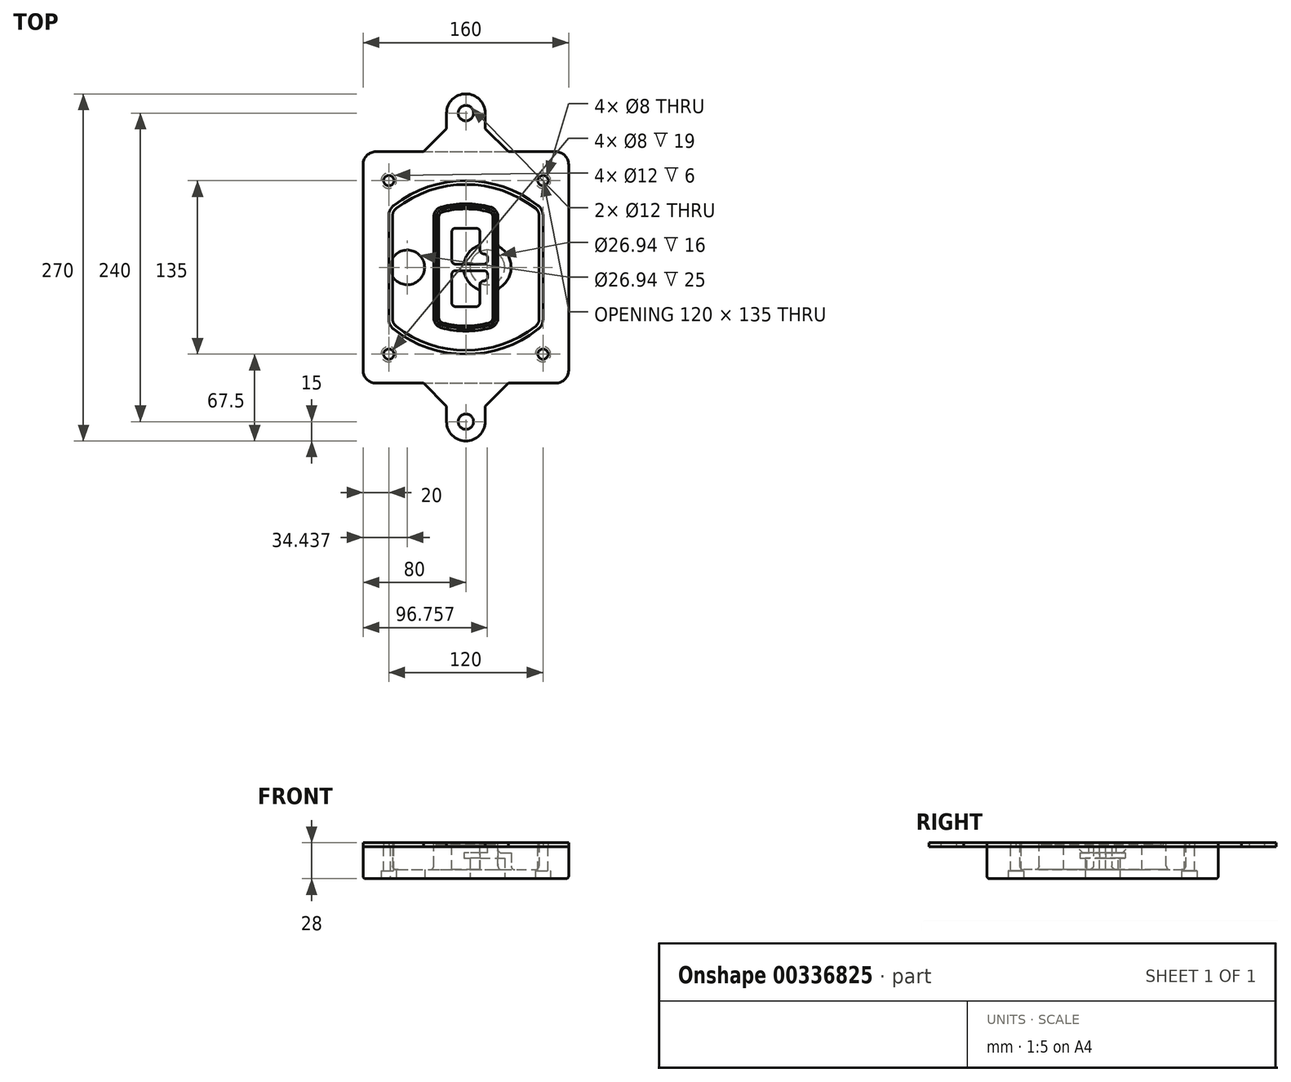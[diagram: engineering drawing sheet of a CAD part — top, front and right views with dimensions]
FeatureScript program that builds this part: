
annotation { "Feature Type Name" : "Feature", "Feature Type Description" : "" }
export const myFeature = defineFeature(function(context is Context, id is Id, definition is map)
    precondition{}
    {
        {
            var Q0;
            Q0=qCreatedBy(makeId("Top.planeOp"),FACE);
            var sketch = newSketch(context, id + "F0", { "sketchPlane" : qUnion([Q0])});
            skPoint(sketch, "E0.rect.middle", {"position": v(0, 0) * mm});
            skLineSegment(sketch, "E1.bottom", {"start": v(-70, -90) * mm, "end": v(70, -90) * mm});
            skLineSegment(sketch, "E1.top", {"start": v(-70, 90) * mm, "end": v(70, 90) * mm});
            skLineSegment(sketch, "E1.left", {"start": v(-80, -80) * mm, "end": v(-80, 80) * mm});
            skLineSegment(sketch, "E1.right", {"start": v(80, -80) * mm, "end": v(80, 80) * mm});
            skLineSegment(sketch, "E2", {"start": v(-80, 90) * mm, "end": v(80, -90) * mm, "construction": true});
            skLineSegment(sketch, "E3", {"start": v(80, 90) * mm, "end": v(-80, -90) * mm, "construction": true});
            skCircle(sketch, "E4", {"center": v(-60, 67.5) * mm, "radius": 4 * mm});
            skCircle(sketch, "E5", {"center": v(60, 67.5) * mm, "radius": 4 * mm});
            skCircle(sketch, "E6", {"center": v(60, -67.5) * mm, "radius": 4 * mm});
            skCircle(sketch, "E7", {"center": v(-60, -67.5) * mm, "radius": 4 * mm});
            skLineSegment(sketch, "E8", {"start": v(-60, 67.5) * mm, "end": v(60, 67.5) * mm, "construction": true});
            skLineSegment(sketch, "E9", {"start": v(60, 67.5) * mm, "end": v(60, -67.5) * mm, "construction": true});
            skLineSegment(sketch, "E10", {"start": v(60, -67.5) * mm, "end": v(-60, -67.5) * mm, "construction": true});
            skLineSegment(sketch, "E11", {"start": v(-60, -67.5) * mm, "end": v(-60, 67.5) * mm, "construction": true});
            skLineSegment(sketch, "E12", {"start": v(-60, 40.3) * mm, "end": v(-60, -40.3) * mm});
            skLineSegment(sketch, "E13", {"start": v(60, 40.3) * mm, "end": v(60, -40.3) * mm});
            skArc(sketch, "E14", {"start": v(56.15, 48.18) * mm, "mid": v(0, 67.5) * mm, "end": v(-56.15, 48.18) * mm});
            skArc(sketch, "E15", {"start": v(-56.15, -48.18) * mm, "mid": v(0, -67.5) * mm, "end": v(56.15, -48.18) * mm});
            skLineSegment(sketch, "E16", {"start": v(-60, 0) * mm, "end": v(60, 0) * mm, "construction": true});
            skPoint(sketch, "E17.visualSharp", {"position": v(-60, -45) * mm});
            skArc(sketch, "E17.filletArc", {"start": v(-60, -40.3) * mm, "mid": v(-58.99, -44.68) * mm, "end": v(-56.15, -48.18) * mm});
            skPoint(sketch, "E18.visualSharp", {"position": v(-60, 45) * mm});
            skArc(sketch, "E18.filletArc", {"start": v(-56.15, 48.18) * mm, "mid": v(-58.99, 44.68) * mm, "end": v(-60, 40.3) * mm});
            skPoint(sketch, "E19.visualSharp", {"position": v(60, 45) * mm});
            skArc(sketch, "E19.filletArc", {"start": v(60, 40.3) * mm, "mid": v(58.99, 44.68) * mm, "end": v(56.15, 48.18) * mm});
            skPoint(sketch, "E20.visualSharp", {"position": v(60, -45) * mm});
            skArc(sketch, "E20.filletArc", {"start": v(56.15, -48.18) * mm, "mid": v(58.99, -44.68) * mm, "end": v(60, -40.3) * mm});
            skPoint(sketch, "E21.visualSharp", {"position": v(-80, 90) * mm});
            skArc(sketch, "E21.filletArc", {"start": v(-70, 90) * mm, "mid": v(-77.07, 87.07) * mm, "end": v(-80, 80) * mm});
            skPoint(sketch, "E22.visualSharp", {"position": v(80, 90) * mm});
            skArc(sketch, "E22.filletArc", {"start": v(80, 80) * mm, "mid": v(77.07, 87.07) * mm, "end": v(70, 90) * mm});
            skPoint(sketch, "E23.visualSharp", {"position": v(80, -90) * mm});
            skArc(sketch, "E23.filletArc", {"start": v(70, -90) * mm, "mid": v(77.07, -87.07) * mm, "end": v(80, -80) * mm});
            skPoint(sketch, "E24.visualSharp", {"position": v(-80, -90) * mm});
            skArc(sketch, "E24.filletArc", {"start": v(-80, -80) * mm, "mid": v(-77.07, -87.07) * mm, "end": v(-70, -90) * mm});
            skArc(sketch, "E25.0", {"start": v(57, 40.3) * mm, "mid": v(56.3, 43.36) * mm, "end": v(54.3, 45.81) * mm});
            skLineSegment(sketch, "E25.1", {"start": v(57, 40.3) * mm, "end": v(57, -40.3) * mm});
            skArc(sketch, "E25.2", {"start": v(54.3, -45.81) * mm, "mid": v(56.3, -43.36) * mm, "end": v(57, -40.3) * mm});
            skArc(sketch, "E25.3", {"start": v(-54.3, -45.81) * mm, "mid": v(0, -64.5) * mm, "end": v(54.3, -45.81) * mm});
            skArc(sketch, "E25.4", {"start": v(-57, -40.3) * mm, "mid": v(-56.3, -43.36) * mm, "end": v(-54.3, -45.81) * mm});
            skArc(sketch, "E25.5", {"start": v(54.3, 45.81) * mm, "mid": v(0, 64.5) * mm, "end": v(-54.3, 45.81) * mm});
            skLineSegment(sketch, "E25.6", {"start": v(-57, 40.3) * mm, "end": v(-57, -40.3) * mm});
            skArc(sketch, "E25.7", {"start": v(-54.3, 45.81) * mm, "mid": v(-56.3, 43.36) * mm, "end": v(-57, 40.3) * mm});
            skArc(sketch, "E26.0", {"start": v(-58.62, 51.33) * mm, "mid": v(-62.58, 46.43) * mm, "end": v(-64, 40.3) * mm});
            skArc(sketch, "E26.1", {"start": v(58.62, 51.33) * mm, "mid": v(0, 71.5) * mm, "end": v(-58.62, 51.33) * mm});
            skArc(sketch, "E26.2", {"start": v(64, 40.3) * mm, "mid": v(62.58, 46.43) * mm, "end": v(58.62, 51.33) * mm});
            skLineSegment(sketch, "E26.3", {"start": v(64, 40.3) * mm, "end": v(64, -40.3) * mm});
            skArc(sketch, "E26.4", {"start": v(58.62, -51.33) * mm, "mid": v(62.58, -46.43) * mm, "end": v(64, -40.3) * mm});
            skLineSegment(sketch, "E26.5", {"start": v(-64, 40.3) * mm, "end": v(-64, -40.3) * mm});
            skArc(sketch, "E26.6", {"start": v(-58.62, -51.33) * mm, "mid": v(0, -71.5) * mm, "end": v(58.62, -51.33) * mm});
            skArc(sketch, "E26.7", {"start": v(-64, -40.3) * mm, "mid": v(-62.58, -46.43) * mm, "end": v(-58.62, -51.33) * mm});
            skSolve(sketch);
        }
        {
            var Q0;
            Q0=makeQuery(id+"F0.imprint","IMPRINT",FACE,{"disambiguationData":[TD([[makeQuery(id+"F0.imprint","IMPRINT",EDGE,{"derivedFrom":sQuery(id+"F0.wireOp",EDGE,"E1.bottom")}),1.0]])]});
            var Q1;
            Q1=makeQuery(id+"F0.imprint","IMPRINT",FACE,{"disambiguationData":[TD([[makeQuery(id+"F0.imprint","IMPRINT",EDGE,{"derivedFrom":sQuery(id+"F0.wireOp",EDGE,"E12")}),1.0]])]});
            var Q2;
            Q2=makeQuery(id+"F0.imprint","IMPRINT",FACE,{"disambiguationData":[TD([[makeQuery(id+"F0.imprint","IMPRINT",EDGE,{"derivedFrom":sQuery(id+"F0.wireOp",EDGE,"E25.0")}),1.0]])]});
            var Q3;
            Q3=makeQuery(id+"F0.imprint","IMPRINT",FACE,{"disambiguationData":[TD([[makeQuery(id+"F0.imprint","IMPRINT",EDGE,{"derivedFrom":sQuery(id+"F0.wireOp",EDGE,"E12")}),-1.0]])]});
            extrude(context, id + "F1", {"entities" : qUnion([Q0, Q1, Q2, Q3]), "oppositeDirection" : true, "depth" : 25 * mm});
        }
        {
            var Q0;
            Q0=makeQuery(id+"F0.imprint","IMPRINT",FACE,{"disambiguationData":[TD([[makeQuery(id+"F0.imprint","IMPRINT",EDGE,{"derivedFrom":sQuery(id+"F0.wireOp",EDGE,"E12")}),1.0]])]});
            extrude(context, id + "F2", {"entities" : qUnion([Q0]), "operationType" : NewBodyOperationType.ADD, "depth" : 3 * mm});
        }
        {
            var Q0;
            Q0=makeQuery(id+"F0.imprint","IMPRINT",FACE,{"disambiguationData":[TD([[makeQuery(id+"F0.imprint","IMPRINT",EDGE,{"derivedFrom":sQuery(id+"F0.wireOp",EDGE,"E25.0")}),1.0]])]});
            extrude(context, id + "F3", {"entities" : qUnion([Q0]), "operationType" : NewBodyOperationType.REMOVE, "oppositeDirection" : true, "depth" : 18 * mm});
        }
        {
            var Q0;
            Q0=makeQuery(id+"F2.opExtrude","CAP_FACE",FACE,{"disambiguationData":[OSD([sQuery(id+"F0.wireOp",EDGE,"E12"),sQuery(id+"F0.wireOp",EDGE,"E13"),sQuery(id+"F0.wireOp",EDGE,"E14"),sQuery(id+"F0.wireOp",EDGE,"E15"),sQuery(id+"F0.wireOp",EDGE,"E17.filletArc"),sQuery(id+"F0.wireOp",EDGE,"E18.filletArc"),sQuery(id+"F0.wireOp",EDGE,"E19.filletArc"),sQuery(id+"F0.wireOp",EDGE,"E20.filletArc"),sQuery(id+"F0.wireOp",EDGE,"E25.0"),sQuery(id+"F0.wireOp",EDGE,"E25.1"),sQuery(id+"F0.wireOp",EDGE,"E25.2"),sQuery(id+"F0.wireOp",EDGE,"E25.3"),sQuery(id+"F0.wireOp",EDGE,"E25.4"),sQuery(id+"F0.wireOp",EDGE,"E25.5"),sQuery(id+"F0.wireOp",EDGE,"E25.6"),sQuery(id+"F0.wireOp",EDGE,"E25.7")])],"isStart":false});
            var sketch = newSketch(context, id + "F4", { "sketchPlane" : qUnion([Q0])});
            skArc(sketch, "E27.0", {"start": v(-19.08, -46.97) * mm, "mid": v(0, -49.5) * mm, "end": v(19.08, -46.97) * mm});
            skArc(sketch, "E28.0", {"start": v(19.08, 46.97) * mm, "mid": v(0, 49.5) * mm, "end": v(-19.08, 46.97) * mm});
            skLineSegment(sketch, "E29", {"start": v(-25, 39.25) * mm, "end": v(-25, -39.25) * mm});
            skLineSegment(sketch, "E30", {"start": v(25, 39.25) * mm, "end": v(25, -39.25) * mm});
            skLineSegment(sketch, "E31", {"start": v(-25, 45.1) * mm, "end": v(25, 45.1) * mm, "construction": true});
            skLineSegment(sketch, "E32", {"start": v(-25, -45.1) * mm, "end": v(25, -45.1) * mm, "construction": true});
            skPoint(sketch, "E33.visualSharp", {"position": v(-25, 45.1) * mm});
            skArc(sketch, "E33.filletArc", {"start": v(-19.08, 46.97) * mm, "mid": v(-23.35, 44.11) * mm, "end": v(-25, 39.25) * mm});
            skPoint(sketch, "E34.visualSharp", {"position": v(25, 45.1) * mm});
            skArc(sketch, "E34.filletArc", {"start": v(25, 39.25) * mm, "mid": v(23.35, 44.11) * mm, "end": v(19.08, 46.97) * mm});
            skPoint(sketch, "E35.visualSharp", {"position": v(25, -45.1) * mm});
            skArc(sketch, "E35.filletArc", {"start": v(19.08, -46.97) * mm, "mid": v(23.35, -44.11) * mm, "end": v(25, -39.25) * mm});
            skPoint(sketch, "E36.visualSharp", {"position": v(-25, -45.1) * mm});
            skArc(sketch, "E36.filletArc", {"start": v(-25, -39.25) * mm, "mid": v(-23.35, -44.11) * mm, "end": v(-19.08, -46.97) * mm});
            skArc(sketch, "E37.0", {"start": v(54.3, 45.81) * mm, "mid": v(0, 64.5) * mm, "end": v(-54.3, 45.81) * mm});
            skArc(sketch, "E37.1", {"start": v(-54.3, 45.81) * mm, "mid": v(-56.3, 43.36) * mm, "end": v(-57, 40.3) * mm});
            skLineSegment(sketch, "E37.2", {"start": v(-57, 40.3) * mm, "end": v(-57, -40.3) * mm});
            skArc(sketch, "E37.3", {"start": v(-57, -40.3) * mm, "mid": v(-56.3, -43.36) * mm, "end": v(-54.3, -45.81) * mm});
            skArc(sketch, "E37.4", {"start": v(-54.3, -45.81) * mm, "mid": v(0, -64.5) * mm, "end": v(54.3, -45.81) * mm});
            skArc(sketch, "E37.5", {"start": v(54.3, -45.81) * mm, "mid": v(56.3, -43.36) * mm, "end": v(57, -40.3) * mm});
            skLineSegment(sketch, "E37.6", {"start": v(57, 40.3) * mm, "end": v(57, -40.3) * mm});
            skArc(sketch, "E37.7", {"start": v(57, 40.3) * mm, "mid": v(56.3, 43.36) * mm, "end": v(54.3, 45.81) * mm});
            skLineSegment(sketch, "E38.0", {"start": v(23, 39.25) * mm, "end": v(23, -39.25) * mm});
            skArc(sketch, "E38.1", {"start": v(18.56, -45.04) * mm, "mid": v(21.76, -42.9) * mm, "end": v(23, -39.25) * mm});
            skArc(sketch, "E38.2", {"start": v(-18.56, -45.04) * mm, "mid": v(0, -47.5) * mm, "end": v(18.56, -45.04) * mm});
            skArc(sketch, "E38.3", {"start": v(-23, -39.25) * mm, "mid": v(-21.76, -42.9) * mm, "end": v(-18.56, -45.04) * mm});
            skLineSegment(sketch, "E38.4", {"start": v(-23, 39.25) * mm, "end": v(-23, -39.25) * mm});
            skArc(sketch, "E38.5", {"start": v(23, 39.25) * mm, "mid": v(21.76, 42.9) * mm, "end": v(18.56, 45.04) * mm});
            skArc(sketch, "E38.6", {"start": v(-18.56, 45.04) * mm, "mid": v(-21.76, 42.9) * mm, "end": v(-23, 39.25) * mm});
            skArc(sketch, "E38.7", {"start": v(18.56, 45.04) * mm, "mid": v(0, 47.5) * mm, "end": v(-18.56, 45.04) * mm});
            skArc(sketch, "E39.0", {"start": v(21, 39.25) * mm, "mid": v(20.18, 41.68) * mm, "end": v(18.04, 43.1) * mm});
            skLineSegment(sketch, "E39.1", {"start": v(21, 39.25) * mm, "end": v(21, -39.25) * mm});
            skArc(sketch, "E39.2", {"start": v(18.04, -43.1) * mm, "mid": v(20.18, -41.68) * mm, "end": v(21, -39.25) * mm});
            skArc(sketch, "E39.3", {"start": v(-18.04, -43.1) * mm, "mid": v(0, -45.5) * mm, "end": v(18.04, -43.1) * mm});
            skArc(sketch, "E39.4", {"start": v(-21, -39.25) * mm, "mid": v(-20.18, -41.68) * mm, "end": v(-18.04, -43.1) * mm});
            skArc(sketch, "E39.5", {"start": v(18.04, 43.1) * mm, "mid": v(0, 45.5) * mm, "end": v(-18.04, 43.1) * mm});
            skLineSegment(sketch, "E39.6", {"start": v(-21, 39.25) * mm, "end": v(-21, -39.25) * mm});
            skArc(sketch, "E39.7", {"start": v(-18.04, 43.1) * mm, "mid": v(-20.18, 41.68) * mm, "end": v(-21, 39.25) * mm});
            skLineSegment(sketch, "E40", {"start": v(-25, 0) * mm, "end": v(25, 0) * mm, "construction": true});
            skLineSegment(sketch, "E41", {"start": v(-11, 5.5) * mm, "end": v(-11, 27.5) * mm});
            skLineSegment(sketch, "E42", {"start": v(-8, 30.5) * mm, "end": v(8, 30.5) * mm});
            skLineSegment(sketch, "E43", {"start": v(11, 27.5) * mm, "end": v(11, 13.5) * mm});
            skLineSegment(sketch, "E44", {"start": v(14, 10.5) * mm, "end": v(14, 10.5) * mm});
            skLineSegment(sketch, "E45", {"start": v(17, 7.5) * mm, "end": v(17, 5.5) * mm});
            skLineSegment(sketch, "E46", {"start": v(14, 2.5) * mm, "end": v(-8, 2.5) * mm});
            skPoint(sketch, "E47.visualSharp", {"position": v(-11, 30.5) * mm});
            skArc(sketch, "E47.filletArc", {"start": v(-8, 30.5) * mm, "mid": v(-10.12, 29.62) * mm, "end": v(-11, 27.5) * mm});
            skPoint(sketch, "E48.visualSharp", {"position": v(11, 30.5) * mm});
            skArc(sketch, "E48.filletArc", {"start": v(11, 27.5) * mm, "mid": v(10.12, 29.62) * mm, "end": v(8, 30.5) * mm});
            skPoint(sketch, "E49.visualSharp", {"position": v(11, 10.5) * mm});
            skArc(sketch, "E49.filletArc", {"start": v(11, 13.5) * mm, "mid": v(11.88, 11.38) * mm, "end": v(14, 10.5) * mm});
            skPoint(sketch, "E50.visualSharp", {"position": v(17, 10.5) * mm});
            skArc(sketch, "E50.filletArc", {"start": v(17, 7.5) * mm, "mid": v(16.12, 9.62) * mm, "end": v(14, 10.5) * mm});
            skPoint(sketch, "E51.visualSharp", {"position": v(17, 2.5) * mm});
            skArc(sketch, "E51.filletArc", {"start": v(14, 2.5) * mm, "mid": v(16.12, 3.38) * mm, "end": v(17, 5.5) * mm});
            skPoint(sketch, "E52.visualSharp", {"position": v(-11, 2.5) * mm});
            skArc(sketch, "E52.filletArc", {"start": v(-11, 5.5) * mm, "mid": v(-10.12, 3.38) * mm, "end": v(-8, 2.5) * mm});
            skLineSegment(sketch, "E53.0.MirrorCS", {"start": v(14, -2.5) * mm, "end": v(-8, -2.5) * mm});
            skArc(sketch, "E54.0.MirrorCS", {"start": v(-11, -5.5) * mm, "mid": v(-10.12, -3.38) * mm, "end": v(-8, -2.5) * mm});
            skLineSegment(sketch, "E55.0.MirrorCS", {"start": v(-11, -5.5) * mm, "end": v(-11, -27.5) * mm});
            skArc(sketch, "E56.0.MirrorCS", {"start": v(-8, -30.5) * mm, "mid": v(-10.12, -29.62) * mm, "end": v(-11, -27.5) * mm});
            skLineSegment(sketch, "E57.0.MirrorCS", {"start": v(-8, -30.5) * mm, "end": v(8, -30.5) * mm});
            skArc(sketch, "E58.0.MirrorCS", {"start": v(11, -27.5) * mm, "mid": v(10.12, -29.62) * mm, "end": v(8, -30.5) * mm});
            skLineSegment(sketch, "E59.0.MirrorCS", {"start": v(11, -27.5) * mm, "end": v(11, -13.5) * mm});
            skArc(sketch, "E60.0.MirrorCS", {"start": v(11, -13.5) * mm, "mid": v(11.88, -11.38) * mm, "end": v(14, -10.5) * mm});
            skArc(sketch, "E61.0.MirrorCS", {"start": v(17, -7.5) * mm, "mid": v(16.12, -9.62) * mm, "end": v(14, -10.5) * mm});
            skLineSegment(sketch, "E62.0.MirrorCS", {"start": v(17, -7.5) * mm, "end": v(17, -5.5) * mm});
            skArc(sketch, "E63.0.MirrorCS", {"start": v(14, -2.5) * mm, "mid": v(16.12, -3.38) * mm, "end": v(17, -5.5) * mm});
            skSolve(sketch);
        }
        {
            var Q0;
            Q0=makeQuery(id+"F4.imprint","IMPRINT",FACE,{"disambiguationData":[TD([[makeQuery(id+"F4.imprint","IMPRINT",EDGE,{"derivedFrom":sQuery(id+"F4.wireOp",EDGE,"E27.0")}),1.0]])]});
            var Q1;
            Q1=makeQuery(id+"F4.imprint","IMPRINT",FACE,{"disambiguationData":[TD([[makeQuery(id+"F4.imprint","IMPRINT",EDGE,{"derivedFrom":sQuery(id+"F4.wireOp",EDGE,"E38.0")}),-1.0]])]});
            var Q2;
            Q2=makeQuery(id+"F4.imprint","IMPRINT",FACE,{"disambiguationData":[TD([[makeQuery(id+"F4.imprint","IMPRINT",EDGE,{"derivedFrom":sQuery(id+"F4.wireOp",EDGE,"E39.0")}),1.0]])]});
            extrude(context, id + "F5", {"entities" : qUnion([Q0, Q1, Q2]), "operationType" : NewBodyOperationType.ADD, "endBound" : BoundingType.UP_TO_NEXT, "oppositeDirection" : true, "depth" : 25 * mm});
        }
        {
            var Q0;
            Q0=makeQuery(id+"F4.imprint","IMPRINT",FACE,{"disambiguationData":[TD([[makeQuery(id+"F4.imprint","IMPRINT",EDGE,{"derivedFrom":sQuery(id+"F4.wireOp",EDGE,"E38.0")}),-1.0]])]});
            extrude(context, id + "F6", {"entities" : qUnion([Q0]), "operationType" : NewBodyOperationType.REMOVE, "oppositeDirection" : true, "depth" : 2 * mm});
        }
        {
            var Q0;
            Q0=makeQuery(id+"F1.opExtrude","CAP_FACE",FACE,{"disambiguationData":[OSD([sQuery(id+"F0.wireOp",EDGE,"E1.bottom"),sQuery(id+"F0.wireOp",EDGE,"E1.top"),sQuery(id+"F0.wireOp",EDGE,"E1.left"),sQuery(id+"F0.wireOp",EDGE,"E1.right"),sQuery(id+"F0.wireOp",EDGE,"E4"),sQuery(id+"F0.wireOp",EDGE,"E5"),sQuery(id+"F0.wireOp",EDGE,"E6"),sQuery(id+"F0.wireOp",EDGE,"E7"),sQuery(id+"F0.wireOp",EDGE,"E21.filletArc"),sQuery(id+"F0.wireOp",EDGE,"E22.filletArc"),sQuery(id+"F0.wireOp",EDGE,"E23.filletArc"),sQuery(id+"F0.wireOp",EDGE,"E24.filletArc")])],"isStart":false});
            var sketch = newSketch(context, id + "F7", { "sketchPlane" : qUnion([Q0])});
            skCircle(sketch, "E64", {"center": v(16.76, 0) * mm, "radius": 13.47 * mm});
            skCircle(sketch, "E65", {"center": v(-45.56, 0) * mm, "radius": 13.47 * mm});
            skLineSegment(sketch, "E66", {"start": v(80, 0) * mm, "end": v(-80, 0) * mm});
            skCircle(sketch, "E67", {"center": v(16.76, 0) * mm, "radius": 18.47 * mm});
            skCircle(sketch, "E68", {"center": v(60, -67.5) * mm, "radius": 6 * mm});
            skCircle(sketch, "E69", {"center": v(-60, -67.5) * mm, "radius": 6 * mm});
            skCircle(sketch, "E70", {"center": v(-60, 67.5) * mm, "radius": 6 * mm});
            skCircle(sketch, "E71", {"center": v(60, 67.5) * mm, "radius": 6 * mm});
            skSolve(sketch);
        }
        {
            var Q0;
            {var subQ1=sQuery(id+"F7.wireOp",EDGE,"E66");var subQ4=sQuery(id+"F7.wireOp",EDGE,"E64");var subQ6=makeQuery(id+"F7.imprint","INTERSECT",VERTEX,{"disambiguationData":[OD(0.0)],"derivedFrom":[subQ4,subQ1]});Q0=makeQuery(id+"F7.imprint","IMPRINT",FACE,{"disambiguationData":[TD([[makeQuery(id+"F7.imprint","IMPRINT",EDGE,{"disambiguationData":[TD([[subQ6,-1.0]])],"derivedFrom":subQ4}),-1.0]])]});}
            var Q1;
            {var subQ0=sQuery(id+"F7.wireOp",EDGE,"E66");var subQ1=sQuery(id+"F7.wireOp",EDGE,"E64");var subQ3=makeQuery(id+"F7.imprint","INTERSECT",VERTEX,{"disambiguationData":[OD(0.0)],"derivedFrom":[subQ1,subQ0]});Q1=makeQuery(id+"F7.imprint","IMPRINT",FACE,{"disambiguationData":[TD([[makeQuery(id+"F7.imprint","IMPRINT",EDGE,{"disambiguationData":[TD([[subQ3,-1.0]])],"derivedFrom":subQ1}),1.0]])]});}
            var Q2;
            {var subQ0=sQuery(id+"F7.wireOp",EDGE,"E66");var subQ1=sQuery(id+"F7.wireOp",EDGE,"E64");var subQ3=makeQuery(id+"F7.imprint","INTERSECT",VERTEX,{"disambiguationData":[OD(0.0)],"derivedFrom":[subQ1,subQ0]});Q2=makeQuery(id+"F7.imprint","IMPRINT",FACE,{"disambiguationData":[TD([[makeQuery(id+"F7.imprint","IMPRINT",EDGE,{"disambiguationData":[TD([[subQ3,1.0]])],"derivedFrom":subQ1}),1.0]])]});}
            var Q3;
            {var subQ1=sQuery(id+"F7.wireOp",EDGE,"E66");var subQ4=sQuery(id+"F7.wireOp",EDGE,"E64");var subQ6=makeQuery(id+"F7.imprint","INTERSECT",VERTEX,{"disambiguationData":[OD(0.0)],"derivedFrom":[subQ4,subQ1]});Q3=makeQuery(id+"F7.imprint","IMPRINT",FACE,{"disambiguationData":[TD([[makeQuery(id+"F7.imprint","IMPRINT",EDGE,{"disambiguationData":[TD([[subQ6,1.0]])],"derivedFrom":subQ4}),-1.0]])]});}
            extrude(context, id + "F8", {"entities" : qUnion([Q0, Q1, Q2, Q3]), "operationType" : NewBodyOperationType.ADD, "oppositeDirection" : true, "depth" : 20 * mm});
        }
        {
            var Q0;
            {var subQ0=sQuery(id+"F7.wireOp",EDGE,"E66");var subQ1=sQuery(id+"F7.wireOp",EDGE,"E64");var subQ3=makeQuery(id+"F7.imprint","INTERSECT",VERTEX,{"disambiguationData":[OD(0.0)],"derivedFrom":[subQ1,subQ0]});Q0=makeQuery(id+"F7.imprint","IMPRINT",FACE,{"disambiguationData":[TD([[makeQuery(id+"F7.imprint","IMPRINT",EDGE,{"disambiguationData":[TD([[subQ3,-1.0]])],"derivedFrom":subQ1}),1.0]])]});}
            var Q1;
            {var subQ0=sQuery(id+"F7.wireOp",EDGE,"E66");var subQ1=sQuery(id+"F7.wireOp",EDGE,"E64");var subQ3=makeQuery(id+"F7.imprint","INTERSECT",VERTEX,{"disambiguationData":[OD(0.0)],"derivedFrom":[subQ1,subQ0]});Q1=makeQuery(id+"F7.imprint","IMPRINT",FACE,{"disambiguationData":[TD([[makeQuery(id+"F7.imprint","IMPRINT",EDGE,{"disambiguationData":[TD([[subQ3,1.0]])],"derivedFrom":subQ1}),1.0]])]});}
            extrude(context, id + "F9", {"entities" : qUnion([Q0, Q1]), "operationType" : NewBodyOperationType.REMOVE, "oppositeDirection" : true, "depth" : 16 * mm});
        }
        {
            var Q0;
            {var subQ0=sQuery(id+"F7.wireOp",EDGE,"E66");var subQ1=sQuery(id+"F7.wireOp",EDGE,"E65");var subQ3=makeQuery(id+"F7.imprint","INTERSECT",VERTEX,{"disambiguationData":[OD(0.0)],"derivedFrom":[subQ1,subQ0]});Q0=makeQuery(id+"F7.imprint","IMPRINT",FACE,{"disambiguationData":[TD([[makeQuery(id+"F7.imprint","IMPRINT",EDGE,{"disambiguationData":[TD([[subQ3,-1.0]])],"derivedFrom":subQ1}),1.0]])]});}
            var Q1;
            {var subQ0=sQuery(id+"F7.wireOp",EDGE,"E66");var subQ1=sQuery(id+"F7.wireOp",EDGE,"E65");var subQ3=makeQuery(id+"F7.imprint","INTERSECT",VERTEX,{"disambiguationData":[OD(0.0)],"derivedFrom":[subQ1,subQ0]});Q1=makeQuery(id+"F7.imprint","IMPRINT",FACE,{"disambiguationData":[TD([[makeQuery(id+"F7.imprint","IMPRINT",EDGE,{"disambiguationData":[TD([[subQ3,1.0]])],"derivedFrom":subQ1}),1.0]])]});}
            extrude(context, id + "F10", {"entities" : qUnion([Q0, Q1]), "operationType" : NewBodyOperationType.REMOVE, "oppositeDirection" : true, "depth" : 25 * mm});
        }
        {
            var Q0;
            Q0=makeQuery(id+"F7.imprint","IMPRINT",FACE,{"disambiguationData":[TD([[makeQuery(id+"F7.imprint","IMPRINT",EDGE,{"derivedFrom":sQuery(id+"F7.wireOp",EDGE,"E68")}),1.0]])]});
            var Q1;
            Q1=makeQuery(id+"F7.imprint","IMPRINT",FACE,{"disambiguationData":[TD([[makeQuery(id+"F7.imprint","IMPRINT",EDGE,{"derivedFrom":makeQuery(id+"F1.opExtrude","CAP_EDGE",EDGE,{"disambiguationData":[OSD([sQuery(id+"F0.wireOp",EDGE,"E5")])],"isStart":false})}),-1.0]])]});
            var Q2;
            Q2=makeQuery(id+"F7.imprint","IMPRINT",FACE,{"disambiguationData":[TD([[makeQuery(id+"F7.imprint","IMPRINT",EDGE,{"derivedFrom":sQuery(id+"F7.wireOp",EDGE,"E69")}),1.0]])]});
            var Q3;
            Q3=makeQuery(id+"F7.imprint","IMPRINT",FACE,{"disambiguationData":[TD([[makeQuery(id+"F7.imprint","IMPRINT",EDGE,{"derivedFrom":makeQuery(id+"F1.opExtrude","CAP_EDGE",EDGE,{"disambiguationData":[OSD([sQuery(id+"F0.wireOp",EDGE,"E4")])],"isStart":false})}),-1.0]])]});
            var Q4;
            Q4=makeQuery(id+"F7.imprint","IMPRINT",FACE,{"disambiguationData":[TD([[makeQuery(id+"F7.imprint","IMPRINT",EDGE,{"derivedFrom":sQuery(id+"F7.wireOp",EDGE,"E70")}),1.0]])]});
            var Q5;
            Q5=makeQuery(id+"F7.imprint","IMPRINT",FACE,{"disambiguationData":[TD([[makeQuery(id+"F7.imprint","IMPRINT",EDGE,{"derivedFrom":makeQuery(id+"F1.opExtrude","CAP_EDGE",EDGE,{"disambiguationData":[OSD([sQuery(id+"F0.wireOp",EDGE,"E7")])],"isStart":false})}),-1.0]])]});
            var Q6;
            Q6=makeQuery(id+"F7.imprint","IMPRINT",FACE,{"disambiguationData":[TD([[makeQuery(id+"F7.imprint","IMPRINT",EDGE,{"derivedFrom":sQuery(id+"F7.wireOp",EDGE,"E71")}),1.0]])]});
            var Q7;
            Q7=makeQuery(id+"F7.imprint","IMPRINT",FACE,{"disambiguationData":[TD([[makeQuery(id+"F7.imprint","IMPRINT",EDGE,{"derivedFrom":makeQuery(id+"F1.opExtrude","CAP_EDGE",EDGE,{"disambiguationData":[OSD([sQuery(id+"F0.wireOp",EDGE,"E6")])],"isStart":false})}),-1.0]])]});
            extrude(context, id + "F11", {"entities" : qUnion([Q0, Q1, Q2, Q3, Q4, Q5, Q6, Q7]), "operationType" : NewBodyOperationType.REMOVE, "oppositeDirection" : true, "depth" : 6 * mm});
        }
        {
            var Q0;
            Q0=makeQuery(id+"F9.boolean.opBoolean","COPY",FACE,{"derivedFrom":makeQuery(id+"F9.opExtrude","CAP_FACE",FACE,{"disambiguationData":[OSD([sQuery(id+"F7.wireOp",EDGE,"E64")])],"isStart":false})});
            var sketch = newSketch(context, id + "F12", { "sketchPlane" : qUnion([Q0])});
            skArc(sketch, "E72.0", {"start": v(11, 17.55) * mm, "mid": v(2.57, 11.82) * mm, "end": v(-1.54, 2.5) * mm});
            skArc(sketch, "E72.1", {"start": v(-1.54, -2.5) * mm, "mid": v(2.57, -11.82) * mm, "end": v(11, -17.55) * mm});
            skLineSegment(sketch, "E73", {"start": v(-1.54, -2.5) * mm, "end": v(14, -2.5) * mm});
            skLineSegment(sketch, "E74.0", {"start": v(14, 2.5) * mm, "end": v(-1.54, 2.5) * mm});
            skArc(sketch, "E74.1", {"start": v(14, 2.5) * mm, "mid": v(16.12, 3.38) * mm, "end": v(17, 5.5) * mm});
            skLineSegment(sketch, "E74.2", {"start": v(17, 7.5) * mm, "end": v(17, 5.5) * mm});
            skArc(sketch, "E74.3", {"start": v(17, 7.5) * mm, "mid": v(16.12, 9.62) * mm, "end": v(14, 10.5) * mm});
            skArc(sketch, "E74.4", {"start": v(11, 13.5) * mm, "mid": v(11.88, 11.38) * mm, "end": v(14, 10.5) * mm});
            skLineSegment(sketch, "E74.5", {"start": v(11, 17.55) * mm, "end": v(11, 13.5) * mm});
            skLineSegment(sketch, "E74.7", {"start": v(14, -2.5) * mm, "end": v(-1.54, -2.5) * mm});
            skArc(sketch, "E74.8", {"start": v(14, -2.5) * mm, "mid": v(16.12, -3.38) * mm, "end": v(17, -5.5) * mm});
            skLineSegment(sketch, "E74.9", {"start": v(17, -7.5) * mm, "end": v(17, -5.5) * mm});
            skArc(sketch, "E74.10", {"start": v(17, -7.5) * mm, "mid": v(16.12, -9.62) * mm, "end": v(14, -10.5) * mm});
            skArc(sketch, "E74.11", {"start": v(11, -13.5) * mm, "mid": v(11.88, -11.38) * mm, "end": v(14, -10.5) * mm});
            skLineSegment(sketch, "E74.12", {"start": v(11, -17.55) * mm, "end": v(11, -13.5) * mm});
            skPoint(sketch, "E75.orphan", {"position": v(11, -27.5) * mm});
            skPoint(sketch, "E76.orphan", {"position": v(-8, -2.5) * mm});
            skPoint(sketch, "E77.orphan", {"position": v(-8, 2.5) * mm});
            skPoint(sketch, "E78.orphan", {"position": v(11, 27.5) * mm});
            skSolve(sketch);
        }
        {
            var Q0;
            {var subQ7=sQuery(id+"F12.wireOp",EDGE,"E72.0");var subQ14=sQuery(id+"F12.wireOp",EDGE,"E72.1");var subQ16=sQuery(id+"F12.wireOp",EDGE,"E74.1");var subQ18=sQuery(id+"F12.wireOp",EDGE,"E74.8");Q0=qUnion([makeQuery(id+"F12.imprint","IMPRINT",FACE,{"disambiguationData":[TD([[makeQuery(id+"F12.imprint","IMPRINT",EDGE,{"derivedFrom":subQ7}),1.0]])]}),makeQuery(id+"F12.imprint","IMPRINT",FACE,{"disambiguationData":[TD([[makeQuery(id+"F12.imprint","IMPRINT",EDGE,{"derivedFrom":subQ14}),1.0]])]}),makeQuery(id+"F12.imprint","IMPRINT",FACE,{"disambiguationData":[TD([[makeQuery(id+"F12.imprint","IMPRINT",EDGE,{"derivedFrom":subQ16}),1.0]])]}),makeQuery(id+"F12.imprint","IMPRINT",FACE,{"disambiguationData":[TD([[makeQuery(id+"F12.imprint","IMPRINT",EDGE,{"derivedFrom":subQ18}),-1.0]])]})]);}
            var Q1;
            Q1=makeQuery(id+"F5.boolean.opBoolean","SPLIT",FACE,{"disambiguationData":[TD([makeQuery(id+"F5.opExtrude","SWEPT_FACE",FACE,{"disambiguationData":[OSD([sQuery(id+"F4.wireOp",EDGE,"E41")])]})])],"derivedFrom":makeQuery(id+"F3.boolean.opBoolean","COPY",FACE,{"derivedFrom":makeQuery(id+"F3.opExtrude","CAP_FACE",FACE,{"disambiguationData":[OSD([sQuery(id+"F0.wireOp",EDGE,"E25.0"),sQuery(id+"F0.wireOp",EDGE,"E25.1"),sQuery(id+"F0.wireOp",EDGE,"E25.2"),sQuery(id+"F0.wireOp",EDGE,"E25.3"),sQuery(id+"F0.wireOp",EDGE,"E25.4"),sQuery(id+"F0.wireOp",EDGE,"E25.5"),sQuery(id+"F0.wireOp",EDGE,"E25.6"),sQuery(id+"F0.wireOp",EDGE,"E25.7")])],"isStart":false})})});
            extrude(context, id + "F13", {"entities" : qUnion([Q0]), "operationType" : NewBodyOperationType.REMOVE, "endBound" : BoundingType.UP_TO_SURFACE, "endBoundEntityFace" : qUnion([Q1]), "depth" : 25 * mm});
        }
        {
            var Q0;
            Q0=makeQuery(id+"F3.boolean.opBoolean","COPY",EDGE,{"derivedFrom":makeQuery(id+"F3.opExtrude","CAP_EDGE",EDGE,{"disambiguationData":[OSD([sQuery(id+"F0.wireOp",EDGE,"E25.6")])],"isStart":false})});
            var Q1;
            Q1=makeQuery(id+"F8.boolean.opBoolean","INTERSECT",EDGE,{"derivedFrom":[makeQuery(id+"F5.opExtrude","SWEPT_FACE",FACE,{"disambiguationData":[OSD([sQuery(id+"F4.wireOp",EDGE,"E30")])]}),makeQuery(id+"F8.opExtrude","CAP_FACE",FACE,{"disambiguationData":[OSD([sQuery(id+"F7.wireOp",EDGE,"E67")])],"isStart":false})]});
            var Q2;
            Q2=makeQuery(id+"F8.boolean.opBoolean","INTERSECT",EDGE,{"disambiguationData":[OD(1.0)],"derivedFrom":[makeQuery(id+"F5.opExtrude","SWEPT_FACE",FACE,{"disambiguationData":[OSD([sQuery(id+"F4.wireOp",EDGE,"E30")])]}),makeQuery(id+"F8.opExtrude","SWEPT_FACE",FACE,{"disambiguationData":[OSD([sQuery(id+"F7.wireOp",EDGE,"E67")])]})]});
            var Q3;
            {var subQ0=sQuery(id+"F4.wireOp",EDGE,"E30");Q3=makeQuery(id+"F8.boolean.opBoolean","SPLIT",EDGE,{"disambiguationData":[TD([makeQuery(id+"F5.opExtrude","SWEPT_FACE",FACE,{"disambiguationData":[OSD([sQuery(id+"F4.wireOp",EDGE,"E35.filletArc")])]})])],"derivedFrom":makeQuery(id+"F5.opExtrude","CAP_EDGE",EDGE,{"disambiguationData":[OSD([subQ0])],"isStart":false})});}
            var Q4;
            {var subQ0=sQuery(id+"F0.wireOp",EDGE,"E25.7");var subQ1=sQuery(id+"F0.wireOp",EDGE,"E25.1");var subQ2=sQuery(id+"F0.wireOp",EDGE,"E25.6");var subQ3=sQuery(id+"F0.wireOp",EDGE,"E25.5");var subQ4=sQuery(id+"F0.wireOp",EDGE,"E25.4");var subQ5=sQuery(id+"F0.wireOp",EDGE,"E25.0");var subQ6=sQuery(id+"F0.wireOp",EDGE,"E25.2");var subQ7=sQuery(id+"F0.wireOp",EDGE,"E25.3");Q4=makeQuery(id+"F8.boolean.opBoolean","INTERSECT",EDGE,{"derivedFrom":[makeQuery(id+"F5.boolean.opBoolean","SPLIT",FACE,{"disambiguationData":[TD([makeQuery(id+"F2.opExtrude","SWEPT_FACE",FACE,{"disambiguationData":[OSD([subQ5])]})])],"derivedFrom":makeQuery(id+"F3.boolean.opBoolean","COPY",FACE,{"derivedFrom":makeQuery(id+"F3.opExtrude","CAP_FACE",FACE,{"disambiguationData":[OSD([subQ5,subQ1,subQ6,subQ7,subQ4,subQ3,subQ2,subQ0])],"isStart":false})})}),makeQuery(id+"F8.opExtrude","SWEPT_FACE",FACE,{"disambiguationData":[OSD([sQuery(id+"F7.wireOp",EDGE,"E67")])]})]});}
            var Q5;
            Q5=makeQuery(id+"F8.boolean.opBoolean","INTERSECT",EDGE,{"disambiguationData":[OD(0.0)],"derivedFrom":[makeQuery(id+"F5.opExtrude","SWEPT_FACE",FACE,{"disambiguationData":[OSD([sQuery(id+"F4.wireOp",EDGE,"E30")])]}),makeQuery(id+"F8.opExtrude","SWEPT_FACE",FACE,{"disambiguationData":[OSD([sQuery(id+"F7.wireOp",EDGE,"E67")])]})]});
            fillet(context, id + "F14", {"entities" : qUnion([Q0, Q1, Q2, Q3, Q4, Q5]), "radius" : 3 * mm, "tangentPropagation" : true, "allowEdgeOverflow" : false});
        }
        {
            var Q0;
            Q0=makeQuery(id+"F1.opExtrude","CAP_EDGE",EDGE,{"disambiguationData":[OSD([sQuery(id+"F0.wireOp",EDGE,"E1.bottom")])],"isStart":false});
            fillet(context, id + "F15", {"entities" : qUnion([Q0]), "radius" : 2 * mm, "tangentPropagation" : true, "allowEdgeOverflow" : false});
        }
        {
            var Q0;
            {var subQ0=sQuery(id+"F0.wireOp",EDGE,"E21.filletArc");var subQ1=sQuery(id+"F0.wireOp",EDGE,"E7");var subQ2=sQuery(id+"F0.wireOp",EDGE,"E6");var subQ3=sQuery(id+"F0.wireOp",EDGE,"E5");var subQ4=sQuery(id+"F0.wireOp",EDGE,"E4");var subQ5=sQuery(id+"F0.wireOp",EDGE,"E22.filletArc");var subQ6=sQuery(id+"F0.wireOp",EDGE,"E1.bottom");var subQ7=sQuery(id+"F0.wireOp",EDGE,"E1.right");var subQ8=sQuery(id+"F0.wireOp",EDGE,"E1.top");var subQ9=sQuery(id+"F0.wireOp",EDGE,"E1.left");var subQ10=sQuery(id+"F0.wireOp",EDGE,"E23.filletArc");var subQ11=sQuery(id+"F0.wireOp",EDGE,"E24.filletArc");Q0=makeQuery(id+"F2.boolean.opBoolean","SPLIT",FACE,{"disambiguationData":[TD([makeQuery(id+"F1.opExtrude","SWEPT_FACE",FACE,{"disambiguationData":[OSD([subQ6])]})])],"derivedFrom":makeQuery(id+"F1.opExtrude","CAP_FACE",FACE,{"disambiguationData":[OSD([subQ6,subQ8,subQ9,subQ7,subQ4,subQ3,subQ2,subQ1,subQ0,subQ5,subQ10,subQ11])],"isStart":true})});}
            var sketch = newSketch(context, id + "F16", { "sketchPlane" : qUnion([Q0])});
            skLineSegment(sketch, "E79.0", {"start": v(-70, 90) * mm, "end": v(70, 90) * mm});
            skArc(sketch, "E79.1", {"start": v(-70, 90) * mm, "mid": v(-77.07, 87.07) * mm, "end": v(-80, 80) * mm});
            skLineSegment(sketch, "E79.2", {"start": v(-80, -80) * mm, "end": v(-80, 80) * mm});
            skArc(sketch, "E79.3", {"start": v(-80, -80) * mm, "mid": v(-77.07, -87.07) * mm, "end": v(-70, -90) * mm});
            skLineSegment(sketch, "E79.4", {"start": v(-70, -90) * mm, "end": v(70, -90) * mm});
            skArc(sketch, "E79.5", {"start": v(70, -90) * mm, "mid": v(77.07, -87.07) * mm, "end": v(80, -80) * mm});
            skLineSegment(sketch, "E79.6", {"start": v(80, -80) * mm, "end": v(80, 80) * mm});
            skArc(sketch, "E79.7", {"start": v(80, 80) * mm, "mid": v(77.07, 87.07) * mm, "end": v(70, 90) * mm});
            skCircle(sketch, "E79.8", {"center": v(-60, 67.5) * mm, "radius": 4 * mm});
            skCircle(sketch, "E79.9", {"center": v(60, 67.5) * mm, "radius": 4 * mm});
            skArc(sketch, "E79.10", {"start": v(56.15, 48.18) * mm, "mid": v(0, 67.5) * mm, "end": v(-56.15, 48.18) * mm});
            skArc(sketch, "E79.11", {"start": v(60, 40.3) * mm, "mid": v(58.99, 44.68) * mm, "end": v(56.15, 48.18) * mm});
            skLineSegment(sketch, "E79.12", {"start": v(60, 40.3) * mm, "end": v(60, -40.3) * mm});
            skArc(sketch, "E79.13", {"start": v(56.15, -48.18) * mm, "mid": v(58.99, -44.68) * mm, "end": v(60, -40.3) * mm});
            skCircle(sketch, "E79.14", {"center": v(60, -67.5) * mm, "radius": 4 * mm});
            skArc(sketch, "E79.15", {"start": v(-56.15, -48.18) * mm, "mid": v(0, -67.5) * mm, "end": v(56.15, -48.18) * mm});
            skCircle(sketch, "E79.16", {"center": v(-60, -67.5) * mm, "radius": 4 * mm});
            skArc(sketch, "E79.17", {"start": v(-60, -40.3) * mm, "mid": v(-58.99, -44.68) * mm, "end": v(-56.15, -48.18) * mm});
            skLineSegment(sketch, "E79.18", {"start": v(-60, 40.3) * mm, "end": v(-60, -40.3) * mm});
            skArc(sketch, "E79.19", {"start": v(-56.15, 48.18) * mm, "mid": v(-58.99, 44.68) * mm, "end": v(-60, 40.3) * mm});
            skLineSegment(sketch, "E80", {"start": v(-33, 90) * mm, "end": v(-15, 108) * mm});
            skLineSegment(sketch, "E81", {"start": v(-15, 108) * mm, "end": v(-15, 120) * mm});
            skLineSegment(sketch, "E82", {"start": v(33, 90) * mm, "end": v(15, 108) * mm});
            skLineSegment(sketch, "E83", {"start": v(15, 108) * mm, "end": v(15, 120) * mm});
            skArc(sketch, "E84", {"start": v(15, 120) * mm, "mid": v(0, 135) * mm, "end": v(-15, 120) * mm});
            skCircle(sketch, "E85", {"center": v(0, 120) * mm, "radius": 6 * mm});
            skLineSegment(sketch, "E86", {"start": v(-80, 0) * mm, "end": v(80, 0) * mm, "construction": true});
            skLineSegment(sketch, "E87.MirrorCS", {"start": v(33, -90) * mm, "end": v(15, -108) * mm});
            skLineSegment(sketch, "E88.MirrorCS", {"start": v(15, -108) * mm, "end": v(15, -120) * mm});
            skArc(sketch, "E89.MirrorCS", {"start": v(15, -120) * mm, "mid": v(0, -135) * mm, "end": v(-15, -120) * mm});
            skCircle(sketch, "E90.MirrorC", {"center": v(0, -120) * mm, "radius": 6 * mm});
            skLineSegment(sketch, "E91.MirrorCS", {"start": v(-33, -90) * mm, "end": v(-15, -108) * mm});
            skLineSegment(sketch, "E92.MirrorCS", {"start": v(-15, -108) * mm, "end": v(-15, -120) * mm});
            skSolve(sketch);
        }
        {
            var Q0;
            Q0 = qSketchRegion(id + "F16", true);
            var Q1;
            {var subQ0=sQuery(id+"F4.wireOp",EDGE,"E63.0.MirrorCS");var subQ1=sQuery(id+"F4.wireOp",EDGE,"E62.0.MirrorCS");var subQ2=sQuery(id+"F4.wireOp",EDGE,"E61.0.MirrorCS");var subQ3=sQuery(id+"F4.wireOp",EDGE,"E60.0.MirrorCS");var subQ4=sQuery(id+"F4.wireOp",EDGE,"E59.0.MirrorCS");var subQ5=sQuery(id+"F4.wireOp",EDGE,"E58.0.MirrorCS");var subQ6=sQuery(id+"F4.wireOp",EDGE,"E57.0.MirrorCS");var subQ7=sQuery(id+"F4.wireOp",EDGE,"E56.0.MirrorCS");var subQ8=sQuery(id+"F4.wireOp",EDGE,"E55.0.MirrorCS");var subQ9=sQuery(id+"F4.wireOp",EDGE,"E54.0.MirrorCS");var subQ10=sQuery(id+"F4.wireOp",EDGE,"E53.0.MirrorCS");var subQ11=sQuery(id+"F4.wireOp",EDGE,"E52.filletArc");var subQ12=sQuery(id+"F4.wireOp",EDGE,"E45");var subQ13=sQuery(id+"F4.wireOp",EDGE,"E43");var subQ14=sQuery(id+"F4.wireOp",EDGE,"E42");var subQ15=sQuery(id+"F4.wireOp",EDGE,"E41");var subQ16=sQuery(id+"F4.wireOp",EDGE,"E46");var subQ17=sQuery(id+"F4.wireOp",EDGE,"E47.filletArc");var subQ18=sQuery(id+"F4.wireOp",EDGE,"E48.filletArc");var subQ19=sQuery(id+"F4.wireOp",EDGE,"E49.filletArc");var subQ20=sQuery(id+"F4.wireOp",EDGE,"E50.filletArc");var subQ21=sQuery(id+"F4.wireOp",EDGE,"E51.filletArc");Q1=makeQuery(id+"F6.boolean.opBoolean","SPLIT",FACE,{"disambiguationData":[TD([makeQuery(id+"F5.opExtrude","SWEPT_FACE",FACE,{"disambiguationData":[OSD([subQ15])]})])],"derivedFrom":makeQuery(id+"F5.opExtrude","CAP_FACE",FACE,{"disambiguationData":[OSD([sQuery(id+"F4.wireOp",EDGE,"E27.0"),sQuery(id+"F4.wireOp",EDGE,"E28.0"),sQuery(id+"F4.wireOp",EDGE,"E29"),sQuery(id+"F4.wireOp",EDGE,"E30"),sQuery(id+"F4.wireOp",EDGE,"E33.filletArc"),sQuery(id+"F4.wireOp",EDGE,"E34.filletArc"),sQuery(id+"F4.wireOp",EDGE,"E35.filletArc"),sQuery(id+"F4.wireOp",EDGE,"E36.filletArc"),subQ15,subQ14,subQ13,subQ12,subQ16,subQ17,subQ18,subQ19,subQ20,subQ21,subQ11,subQ10,subQ9,subQ8,subQ7,subQ6,subQ5,subQ4,subQ3,subQ2,subQ1,subQ0])],"isStart":true})});}
            extrude(context, id + "F17", {"entities" : qUnion([Q0]), "endBound" : BoundingType.UP_TO_SURFACE, "endBoundEntityFace" : qUnion([Q1]), "depth" : 25 * mm});
        }
    });
